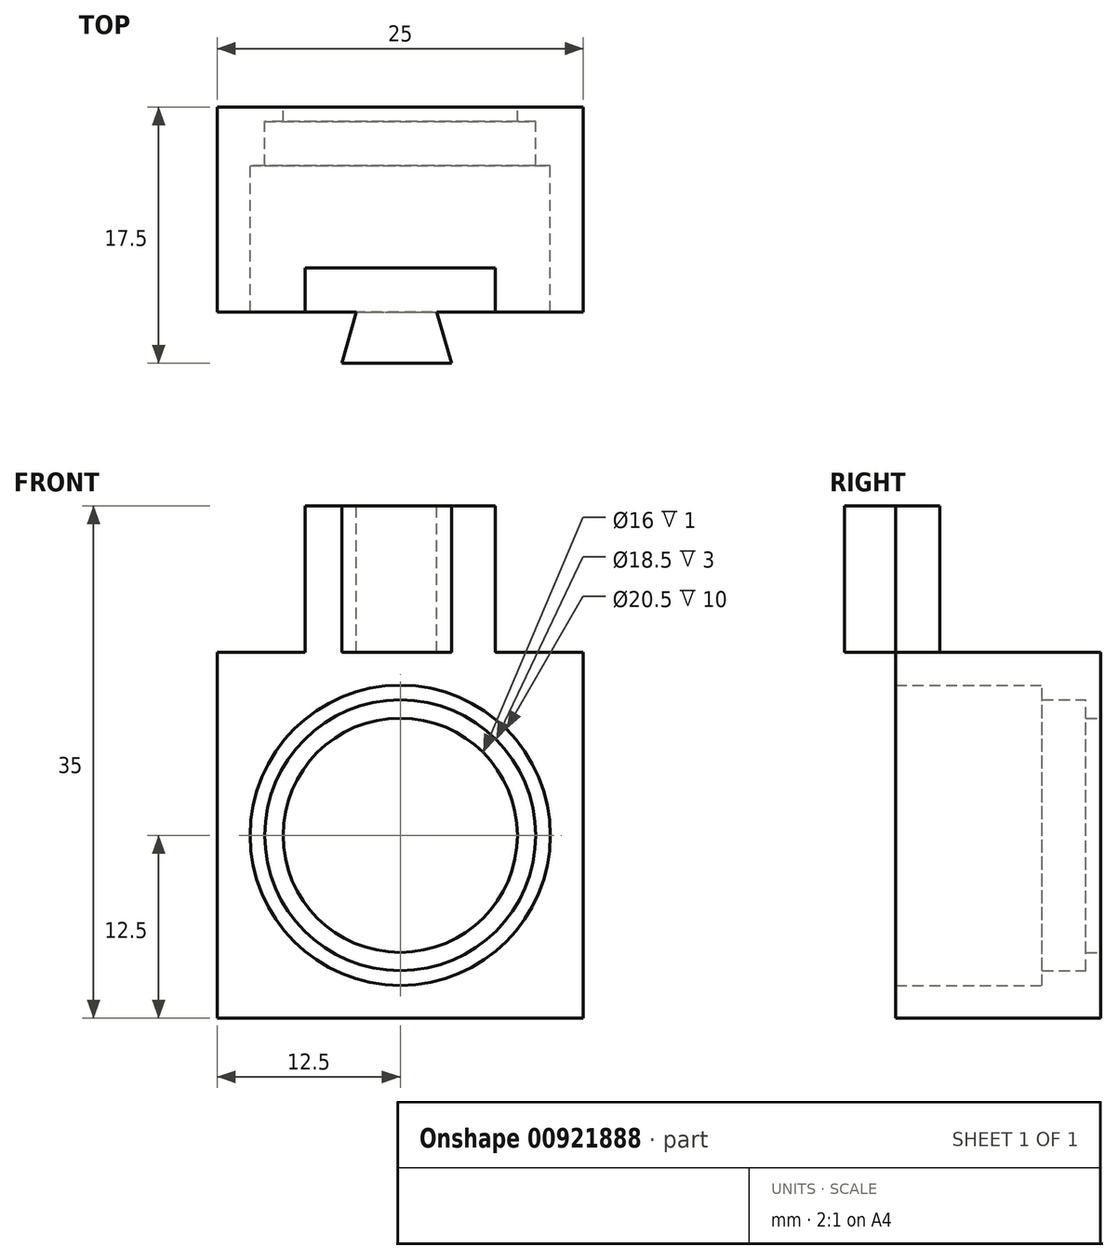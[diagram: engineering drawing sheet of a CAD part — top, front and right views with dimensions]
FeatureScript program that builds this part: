
annotation { "Feature Type Name" : "Feature", "Feature Type Description" : "" }
export const myFeature = defineFeature(function(context is Context, id is Id, definition is map)
    precondition{}
    {
        {
            var Q0;
            Q0=qCreatedBy(makeId("Front.planeOp"),FACE);
            var sketch = newSketch(context, id + "F0", { "sketchPlane" : qUnion([Q0])});
            skLineSegment(sketch, "E0.bottom", {"start": v(0, 0) * mm, "end": v(25, 0) * mm});
            skLineSegment(sketch, "E0.top", {"start": v(0, 25) * mm, "end": v(25, 25) * mm});
            skLineSegment(sketch, "E0.left", {"start": v(0, 0) * mm, "end": v(0, 25) * mm});
            skLineSegment(sketch, "E0.right", {"start": v(25, 0) * mm, "end": v(25, 25) * mm});
            skCircle(sketch, "E1", {"center": v(12.5, 12.5) * mm, "radius": 10.25 * mm});
            skCircle(sketch, "E2", {"center": v(12.5, 12.5) * mm, "radius": 9.25 * mm});
            skCircle(sketch, "E3", {"center": v(12.5, 12.5) * mm, "radius": 8 * mm});
            skSolve(sketch);
        }
        {
            var Q0;
            Q0=makeQuery(id+"F0.imprint","IMPRINT",FACE,{"disambiguationData":[TD([[makeQuery(id+"F0.imprint","IMPRINT",EDGE,{"derivedFrom":sQuery(id+"F0.wireOp",EDGE,"E0.bottom")}),1.0]])]});
            var Q1;
            Q1=makeQuery(id+"F0.imprint","IMPRINT",FACE,{"disambiguationData":[TD([[makeQuery(id+"F0.imprint","IMPRINT",EDGE,{"derivedFrom":sQuery(id+"F0.wireOp",EDGE,"E1")}),1.0]])]});
            var Q2;
            Q2=makeQuery(id+"F0.imprint","IMPRINT",FACE,{"disambiguationData":[TD([[makeQuery(id+"F0.imprint","IMPRINT",EDGE,{"derivedFrom":sQuery(id+"F0.wireOp",EDGE,"E2")}),1.0]])]});
            extrude(context, id + "F1", {"entities" : qUnion([Q0, Q1, Q2]), "depth" : 1 * mm, "offsetDistance" : 25 * mm});
        }
        {
            var Q0;
            Q0=makeQuery(id+"F1.opExtrude","CAP_FACE",FACE,{"disambiguationData":[OSD([sQuery(id+"F0.wireOp",EDGE,"E0.bottom"),sQuery(id+"F0.wireOp",EDGE,"E0.top"),sQuery(id+"F0.wireOp",EDGE,"E0.left"),sQuery(id+"F0.wireOp",EDGE,"E0.right"),sQuery(id+"F0.wireOp",EDGE,"E3")])],"isStart":false});
            var sketch = newSketch(context, id + "F2", { "sketchPlane" : qUnion([Q0])});
            skCircle(sketch, "E4", {"center": v(12.5, 12.5) * mm, "radius": 9.25 * mm});
            skSolve(sketch);
        }
        {
            var Q0;
            Q0=makeQuery(id+"F2.imprint","IMPRINT",FACE,{"disambiguationData":[TD([[makeQuery(id+"F2.imprint","IMPRINT",EDGE,{"derivedFrom":sQuery(id+"F2.wireOp",EDGE,"E4")}),-1.0]])]});
            extrude(context, id + "F3", {"entities" : qUnion([Q0]), "operationType" : NewBodyOperationType.ADD, "depth" : 3 * mm, "offsetDistance" : 25 * mm});
        }
        {
            var Q0;
            Q0=makeQuery(id+"F3.opExtrude","CAP_FACE",FACE,{"disambiguationData":[OSD([sQuery(id+"F0.wireOp",EDGE,"E0.bottom"),sQuery(id+"F0.wireOp",EDGE,"E0.top"),sQuery(id+"F0.wireOp",EDGE,"E0.left"),sQuery(id+"F0.wireOp",EDGE,"E0.right"),sQuery(id+"F2.wireOp",EDGE,"E4")])],"isStart":false});
            var sketch = newSketch(context, id + "F4", { "sketchPlane" : qUnion([Q0])});
            skCircle(sketch, "E5", {"center": v(12.5, 12.5) * mm, "radius": 10.25 * mm});
            skSolve(sketch);
        }
        {
            var Q0;
            Q0=makeQuery(id+"F4.imprint","IMPRINT",FACE,{"disambiguationData":[TD([[makeQuery(id+"F4.imprint","IMPRINT",EDGE,{"derivedFrom":sQuery(id+"F4.wireOp",EDGE,"E5")}),-1.0]])]});
            extrude(context, id + "F5", {"entities" : qUnion([Q0]), "operationType" : NewBodyOperationType.ADD, "depth" : 10 * mm, "offsetDistance" : 25 * mm});
        }
        {
            var Q0;
            {var subQ0=sQuery(id+"F0.wireOp",EDGE,"E0.top");Q0=makeQuery(id+"F5.boolean.opBoolean","MERGE",FACE,{"derivedFrom":[makeQuery(id+"F3.boolean.opBoolean","MERGE",FACE,{"derivedFrom":[makeQuery(id+"F1.opExtrude","SWEPT_FACE",FACE,{"disambiguationData":[OSD([subQ0])]}),makeQuery(id+"F3.opExtrude","SWEPT_FACE",FACE,{"disambiguationData":[OSD([subQ0])]})]}),makeQuery(id+"F5.opExtrude","SWEPT_FACE",FACE,{"disambiguationData":[OSD([subQ0])]})]});}
            var sketch = newSketch(context, id + "F6", { "sketchPlane" : qUnion([Q0])});
            skLineSegment(sketch, "E6", {"start": v(6, -14) * mm, "end": v(6, -11) * mm});
            skLineSegment(sketch, "E7", {"start": v(6, -11) * mm, "end": v(19, -11) * mm});
            skLineSegment(sketch, "E8", {"start": v(19, -11) * mm, "end": v(19, -14) * mm});
            skSolve(sketch);
        }
        {
            var Q0;
            {var subQ0=sQuery(id+"F6.wireOp",EDGE,"E6");Q0=makeQuery(id+"F6.imprint","IMPRINT",FACE,{"disambiguationData":[TD([[makeQuery(id+"F6.imprint","IMPRINT",EDGE,{"derivedFrom":subQ0}),-1.0]])]});}
            extrude(context, id + "F7", {"entities" : qUnion([Q0]), "operationType" : NewBodyOperationType.ADD, "depth" : 10 * mm, "offsetDistance" : 25 * mm});
        }
        {
            var Q0;
            {var subQ0=sQuery(id+"F0.wireOp",EDGE,"E0.top");Q0=makeQuery(id+"F7.boolean.opBoolean","MERGE",FACE,{"derivedFrom":[makeQuery(id+"F5.opExtrude","CAP_FACE",FACE,{"disambiguationData":[OSD([sQuery(id+"F0.wireOp",EDGE,"E0.bottom"),subQ0,sQuery(id+"F0.wireOp",EDGE,"E0.left"),sQuery(id+"F0.wireOp",EDGE,"E0.right"),sQuery(id+"F4.wireOp",EDGE,"E5")])],"isStart":false}),makeQuery(id+"F7.opExtrude","SWEPT_FACE",FACE,{"disambiguationData":[OSD([subQ0])]})]});}
            var sketch = newSketch(context, id + "F8", { "sketchPlane" : qUnion([Q0])});
            skLineSegment(sketch, "E9", {"start": v(8.5, 35) * mm, "end": v(8.5, 25) * mm});
            skLineSegment(sketch, "E10", {"start": v(8.5, 25) * mm, "end": v(16, 25) * mm});
            skLineSegment(sketch, "E11", {"start": v(16, 25) * mm, "end": v(16, 35) * mm});
            skSolve(sketch);
        }
        {
            var Q0;
            {var subQ0=sQuery(id+"F8.wireOp",EDGE,"E9");Q0=makeQuery(id+"F8.imprint","IMPRINT",FACE,{"disambiguationData":[TD([[makeQuery(id+"F8.imprint","IMPRINT",EDGE,{"derivedFrom":subQ0}),1.0]])]});}
            extrude(context, id + "F9", {"entities" : qUnion([Q0]), "operationType" : NewBodyOperationType.ADD, "depth" : 3.5 * mm, "offsetDistance" : 25 * mm});
        }
        {
            var Q0;
            {var subQ0=sQuery(id+"F0.wireOp",EDGE,"E0.top");Q0=makeQuery(id+"F9.boolean.opBoolean","MERGE",FACE,{"derivedFrom":[makeQuery(id+"F7.opExtrude","CAP_FACE",FACE,{"disambiguationData":[OSD([subQ0,sQuery(id+"F6.wireOp",EDGE,"E6"),sQuery(id+"F6.wireOp",EDGE,"E7"),sQuery(id+"F6.wireOp",EDGE,"E8")])],"isStart":false}),makeQuery(id+"F9.opExtrude","SWEPT_FACE",FACE,{"disambiguationData":[OSD([subQ0])]})]});}
            var sketch = newSketch(context, id + "F10", { "sketchPlane" : qUnion([Q0])});
            skLineSegment(sketch, "E12", {"start": v(16, -17.5) * mm, "end": v(15, -14) * mm});
            skLineSegment(sketch, "E13", {"start": v(15, -14) * mm, "end": v(16, -14) * mm});
            skLineSegment(sketch, "E14", {"start": v(8.5, -17.5) * mm, "end": v(9.5, -14) * mm});
            skLineSegment(sketch, "E15", {"start": v(9.5, -14) * mm, "end": v(8.5, -14) * mm});
            skSolve(sketch);
        }
        {
            var Q0;
            Q0=makeQuery(id+"F10.imprint","IMPRINT",FACE,{"disambiguationData":[TD([[makeQuery(id+"F10.imprint","IMPRINT",EDGE,{"derivedFrom":sQuery(id+"F10.wireOp",EDGE,"E14")}),1.0]])]});
            extrude(context, id + "F11", {"entities" : qUnion([Q0]), "operationType" : NewBodyOperationType.REMOVE, "oppositeDirection" : true, "depth" : 10 * mm, "offsetDistance" : 25 * mm});
        }
        {
            var Q0;
            Q0=makeQuery(id+"F10.imprint","IMPRINT",FACE,{"disambiguationData":[TD([[makeQuery(id+"F10.imprint","IMPRINT",EDGE,{"derivedFrom":sQuery(id+"F10.wireOp",EDGE,"E12")}),-1.0]])]});
            extrude(context, id + "F12", {"entities" : qUnion([Q0]), "operationType" : NewBodyOperationType.REMOVE, "oppositeDirection" : true, "depth" : 10 * mm, "offsetDistance" : 25 * mm});
        }
    });
